# Revit family: Lighting Fixture Generic Model
name_source: partatom
category: Lighting Fixtures
units: mm (PartAtom-declared; Revit-internal decimal feet)

## family parameters
Always vertical = Yes
Cut with Voids When Loaded = No
Light Source = Yes
Maintain Annotation Orientation = No
OmniClass Number = 23.80.70.00
OmniClass Title = Lighting
Part Type = Normal
Room Calculation Point = No
Round Connector Dimension = Use Diameter
Shared = No
Work Plane-Based = No

## types (4) — shared parameters
CRI = 90
Color Filter = 16777215
Default Elevation = 0' - 0"
Description = Hexagon LED Light
Dimming Lamp Color Temperature Shift = <None>
IP Rating = 20
Input Voltage = 120-277V, 50/60 Hz
Lamp = LED
Load Classification = Lighting
Manufacturer = Above All Lighting
Photometric Web File = HEX-4024-30901.ies
Power Factor = 0.9
Tilt Angle = 90.00°
URL = https://www.abovealllighting.com
luminaire = Yes

## per-type parameters (varying)
| type | A | B | L | Model | Wattage Comments |
| HEX_40W_4000K | 1' - 8 1/2" | 1' - 11 11/16" | 0' - 11 27/32" | HEX-4024-40901-SMK | 40W |
| HEX_25W_4000K | 1' - 4 13/32" | 1' - 6 15/16" | 0' - 9 15/32" | HEX-2519-40901-SMK | 25W |
| HEX_90W_4000K | 2' - 6 11/16" | 2' - 11 7/16" | 1' - 5 23/32" | HEX-9035-40901-SMK | 90W |
| HEX_180W_4000K | 3' - 4 29/32" | 3' - 11 7/32" | 1' - 11 5/8" | HEX-18047-40901-SMK | 180W |

## geometry (parser evidence)
native form markers: Sweep x2
no freeform markers — native parametric forms only
